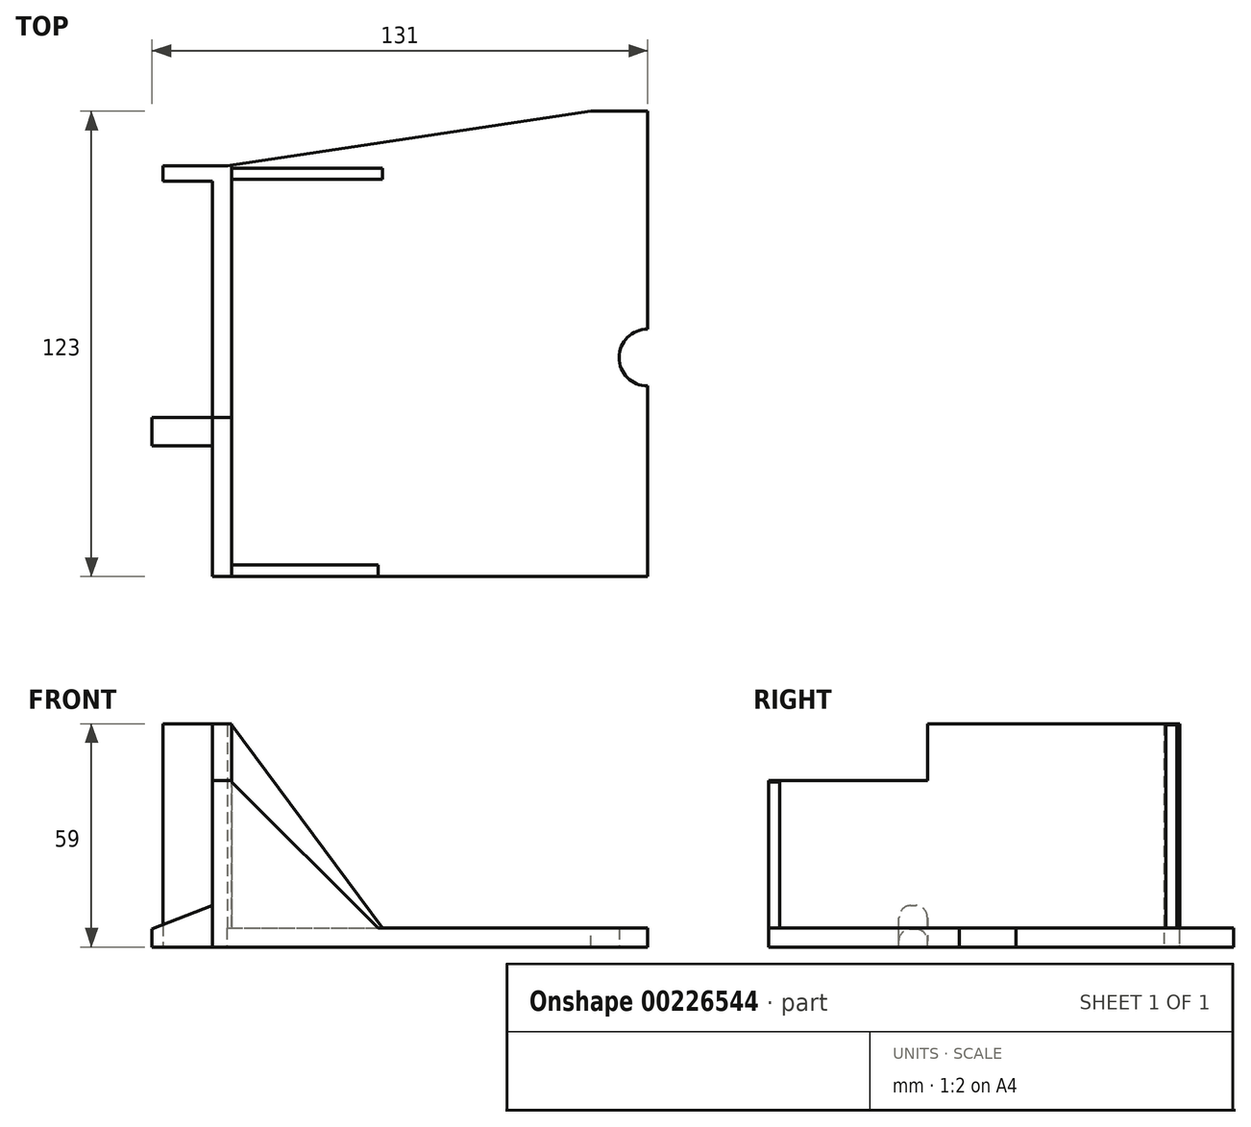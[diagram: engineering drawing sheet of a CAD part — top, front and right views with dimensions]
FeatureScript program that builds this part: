
annotation { "Feature Type Name" : "Feature", "Feature Type Description" : "" }
export const myFeature = defineFeature(function(context is Context, id is Id, definition is map)
    precondition{}
    {
        {
            var Q0;
            Q0=qCreatedBy(makeId("Top.planeOp"),FACE);
            var sketch = newSketch(context, id + "F0", { "sketchPlane" : qUnion([Q0])});
            skLineSegment(sketch, "E0.bottom", {"start": v(57.5, 61.5) * mm, "end": v(-57.5, 61.5) * mm});
            skLineSegment(sketch, "E0.top", {"start": v(57.5, -61.5) * mm, "end": v(-57.5, -61.5) * mm});
            skLineSegment(sketch, "E0.left", {"start": v(57.5, 61.5) * mm, "end": v(57.5, -61.5) * mm});
            skLineSegment(sketch, "E0.right", {"start": v(-57.5, 61.5) * mm, "end": v(-57.5, -61.5) * mm});
            skPoint(sketch, "E0.middle", {"position": v(0, 0) * mm});
            skCircle(sketch, "E1", {"center": v(57.5, -3.62) * mm, "radius": 7.5 * mm});
            skSolve(sketch);
        }
        {
            var Q0;
            {var subQ4=sQuery(id+"F0.wireOp",EDGE,"E0.bottom");Q0=makeQuery(id+"F0.imprint","IMPRINT",FACE,{"disambiguationData":[TD([[makeQuery(id+"F0.imprint","IMPRINT",EDGE,{"derivedFrom":subQ4}),1.0]])]});}
            extrude(context, id + "F1", {"entities" : qUnion([Q0]), "depth" : 5 * mm});
        }
        {
            var Q0;
            Q0=makeQuery(id+"F1.opExtrude","SWEPT_EDGE",EDGE,{"disambiguationData":[OSD([sQuery(id+"F0.wireOp",EDGE,"E0.bottom"),sQuery(id+"F0.wireOp",EDGE,"E0.right")])]});
            chamfer(context, id + "F2", {"entities" : qUnion([Q0]), "chamferType" : ChamferType.TWO_OFFSETS, "width1" : 15 * mm, "oppositeDirection" : false, "width2" : 100 * mm, "tangentPropagation" : true});
        }
        {
            var Q0;
            Q0=makeQuery(id+"F1.opExtrude","CAP_FACE",FACE,{"disambiguationData":[OSD([sQuery(id+"F0.wireOp",EDGE,"E0.bottom"),sQuery(id+"F0.wireOp",EDGE,"E0.top"),sQuery(id+"F0.wireOp",EDGE,"E0.left"),sQuery(id+"F0.wireOp",EDGE,"E0.right"),sQuery(id+"F0.wireOp",EDGE,"E1")])],"isStart":false});
            var sketch = newSketch(context, id + "F3", { "sketchPlane" : qUnion([Q0])});
            skLineSegment(sketch, "E2.bottom", {"start": v(-57.5, 46.5) * mm, "end": v(-52.5, 46.5) * mm});
            skLineSegment(sketch, "E2.top", {"start": v(-57.5, -61.5) * mm, "end": v(-52.5, -61.5) * mm});
            skLineSegment(sketch, "E2.left", {"start": v(-57.5, 46.5) * mm, "end": v(-57.5, -61.5) * mm});
            skLineSegment(sketch, "E2.right", {"start": v(-52.5, 46.5) * mm, "end": v(-52.5, -61.5) * mm});
            skLineSegment(sketch, "E3.bottom", {"start": v(-52.5, 46.5) * mm, "end": v(-52.5, 46.5) * mm});
            skLineSegment(sketch, "E3.top", {"start": v(-52.5, 47.25) * mm, "end": v(-52.5, 47.25) * mm});
            skLineSegment(sketch, "E3.left", {"start": v(-52.5, 46.5) * mm, "end": v(-52.5, 47.25) * mm});
            skLineSegment(sketch, "E3.right", {"start": v(-52.5, 46.5) * mm, "end": v(-52.5, 47.25) * mm});
            skSolve(sketch);
        }
        {
            var Q0;
            Q0=makeQuery(id+"F3.imprint","IMPRINT",FACE,{"disambiguationData":[TD([[makeQuery(id+"F3.imprint","IMPRINT",EDGE,{"derivedFrom":sQuery(id+"F3.wireOp",EDGE,"E2.bottom")}),-1.0]])]});
            extrude(context, id + "F4", {"entities" : qUnion([Q0]), "operationType" : NewBodyOperationType.ADD, "depth" : 54 * mm});
        }
        {
            var Q0;
            Q0=makeQuery(id+"F4.opExtrude","SWEPT_FACE",FACE,{"disambiguationData":[OSD([sQuery(id+"F3.wireOp",EDGE,"E2.bottom")])]});
            var Q1;
            Q1=makeQuery(id+"F4.opExtrude","SWEPT_EDGE",EDGE,{"disambiguationData":[OSD([sQuery(id+"F0.wireOp",EDGE,"E0.bottom"),sQuery(id+"F0.wireOp",EDGE,"E0.top"),sQuery(id+"F0.wireOp",EDGE,"E0.left"),sQuery(id+"F0.wireOp",EDGE,"E0.right"),sQuery(id+"F0.wireOp",EDGE,"E1"),sQuery(id+"F3.wireOp",EDGE,"E2.bottom"),sQuery(id+"F3.wireOp",EDGE,"E2.left")])]});
            revolve(context, id + "F5", {"operationType" : NewBodyOperationType.ADD, "entities" : qUnion([Q0]), "axis" : qUnion([Q1]), "revolveType" : RevolveType.ONE_DIRECTION, "oppositeDirection" : true, "angle" : 7.98 * degree});
        }
        {
            var Q0;
            Q0=makeQuery(id+"F4.opExtrude","SWEPT_FACE",FACE,{"disambiguationData":[OSD([sQuery(id+"F3.wireOp",EDGE,"E2.right")])]});
            var sketch = newSketch(context, id + "F6", { "sketchPlane" : qUnion([Q0])});
            skLineSegment(sketch, "E4.bottom", {"start": v(-61.5, 59) * mm, "end": v(-19.5, 59) * mm});
            skLineSegment(sketch, "E4.top", {"start": v(-61.5, 44) * mm, "end": v(-19.5, 44) * mm});
            skLineSegment(sketch, "E4.left", {"start": v(-61.5, 59) * mm, "end": v(-61.5, 44) * mm});
            skLineSegment(sketch, "E4.right", {"start": v(-19.5, 59) * mm, "end": v(-19.5, 44) * mm});
            skSolve(sketch);
        }
        {
            var Q0;
            Q0=makeQuery(id+"F6.imprint","IMPRINT",FACE,{"disambiguationData":[TD([[makeQuery(id+"F6.imprint","IMPRINT",EDGE,{"derivedFrom":sQuery(id+"F6.wireOp",EDGE,"E4.bottom")}),1.0]])]});
            extrude(context, id + "F7", {"entities" : qUnion([Q0]), "operationType" : NewBodyOperationType.REMOVE, "oppositeDirection" : true, "depth" : 25 * mm});
        }
        {
            var Q0;
            Q0=makeQuery(id+"F4.boolean.opBoolean","MERGE",FACE,{"derivedFrom":[makeQuery(id+"F1.opExtrude","SWEPT_FACE",FACE,{"disambiguationData":[OSD([sQuery(id+"F0.wireOp",EDGE,"E0.right")])]}),makeQuery(id+"F4.opExtrude","SWEPT_FACE",FACE,{"disambiguationData":[OSD([sQuery(id+"F3.wireOp",EDGE,"E2.left")])]})]});
            var sketch = newSketch(context, id + "F8", { "sketchPlane" : qUnion([Q0])});
            skLineSegment(sketch, "E5.bottom", {"start": v(19.5, 0) * mm, "end": v(27, 0) * mm});
            skLineSegment(sketch, "E5.top", {"start": v(19.5, 11) * mm, "end": v(27, 11) * mm});
            skLineSegment(sketch, "E5.left", {"start": v(19.5, 0) * mm, "end": v(19.5, 11) * mm});
            skLineSegment(sketch, "E5.right", {"start": v(27, 0) * mm, "end": v(27, 11) * mm});
            skSolve(sketch);
        }
        {
            var Q0;
            Q0=makeQuery(id+"F8.imprint","IMPRINT",FACE,{"disambiguationData":[TD([[makeQuery(id+"F8.imprint","IMPRINT",EDGE,{"derivedFrom":sQuery(id+"F8.wireOp",EDGE,"E5.bottom")}),1.0]])]});
            extrude(context, id + "F9", {"entities" : qUnion([Q0]), "operationType" : NewBodyOperationType.ADD, "depth" : 16 * mm});
        }
        {
            var Q0;
            Q0=makeQuery(id+"F9.opExtrude","CAP_EDGE",EDGE,{"disambiguationData":[OSD([sQuery(id+"F8.wireOp",EDGE,"E5.top")])],"isStart":false});
            chamfer(context, id + "F10", {"entities" : qUnion([Q0]), "chamferType" : ChamferType.TWO_OFFSETS, "width1" : 16.1 * mm, "oppositeDirection" : false, "width2" : 6.2 * mm, "tangentPropagation" : true});
        }
        {
            var Q0;
            Q0=makeQuery(id+"F10.opChamfer","BLEND_EDGE",EDGE,{"blendedFrom":[makeQuery(id+"F9.opExtrude","CAP_EDGE",EDGE,{"disambiguationData":[OSD([sQuery(id+"F8.wireOp",EDGE,"E5.top")])],"isStart":false}),makeQuery(id+"F9.opExtrude","SWEPT_FACE",FACE,{"disambiguationData":[OSD([sQuery(id+"F8.wireOp",EDGE,"E5.right")])]})],"blendedInto":[makeQuery(id+"F9.opExtrude","SWEPT_FACE",FACE,{"disambiguationData":[OSD([sQuery(id+"F8.wireOp",EDGE,"E5.right")])]})]});
            var Q1;
            Q1=makeQuery(id+"F10.opChamfer","BLEND_EDGE",EDGE,{"blendedFrom":[makeQuery(id+"F9.opExtrude","CAP_EDGE",EDGE,{"disambiguationData":[OSD([sQuery(id+"F8.wireOp",EDGE,"E5.top")])],"isStart":false}),makeQuery(id+"F9.opExtrude","SWEPT_FACE",FACE,{"disambiguationData":[OSD([sQuery(id+"F8.wireOp",EDGE,"E5.left")])]})],"blendedInto":[makeQuery(id+"F9.opExtrude","SWEPT_FACE",FACE,{"disambiguationData":[OSD([sQuery(id+"F8.wireOp",EDGE,"E5.left")])]})]});
            fillet(context, id + "F11", {"entities" : qUnion([Q0, Q1]), "radius" : 3 * mm, "tangentPropagation" : true, "allowEdgeOverflow" : false});
        }
        {
            var Q0;
            Q0=qCreatedBy(makeId("Top.planeOp"),FACE);
            var sketch = newSketch(context, id + "F12", { "sketchPlane" : qUnion([Q0])});
            skLineSegment(sketch, "E6.bottom", {"start": v(-52.66, 43.06) * mm, "end": v(-70.66, 43.06) * mm});
            skLineSegment(sketch, "E6.top", {"start": v(-52.66, 47.06) * mm, "end": v(-70.66, 47.06) * mm});
            skLineSegment(sketch, "E6.left", {"start": v(-52.66, 43.06) * mm, "end": v(-52.66, 47.06) * mm});
            skLineSegment(sketch, "E6.right", {"start": v(-70.66, 43.06) * mm, "end": v(-70.66, 47.06) * mm});
            skSolve(sketch);
        }
        {
            var Q0;
            Q0 = qSketchRegion(id + "F12", true);
            extrude(context, id + "F13", {"entities" : qUnion([Q0]), "operationType" : NewBodyOperationType.ADD, "depth" : 59 * mm});
        }
        {
            var Q0;
            Q0=makeQuery(id+"F1.opExtrude","CAP_FACE",FACE,{"disambiguationData":[OSD([sQuery(id+"F0.wireOp",EDGE,"E0.bottom"),sQuery(id+"F0.wireOp",EDGE,"E0.top"),sQuery(id+"F0.wireOp",EDGE,"E0.left"),sQuery(id+"F0.wireOp",EDGE,"E0.right"),sQuery(id+"F0.wireOp",EDGE,"E1")])],"isStart":false});
            var sketch = newSketch(context, id + "F14", { "sketchPlane" : qUnion([Q0])});
            skLineSegment(sketch, "E7.bottom", {"start": v(-12.5, -61.5) * mm, "end": v(-52.5, -61.5) * mm});
            skLineSegment(sketch, "E7.top", {"start": v(-12.5, -58.5) * mm, "end": v(-52.5, -58.5) * mm});
            skLineSegment(sketch, "E7.left", {"start": v(-12.5, -61.5) * mm, "end": v(-12.5, -58.5) * mm});
            skLineSegment(sketch, "E7.right", {"start": v(-52.5, -61.5) * mm, "end": v(-52.5, -58.5) * mm});
            skLineSegment(sketch, "E8.bottom", {"start": v(-52.5, 46.5) * mm, "end": v(-12.5, 46.5) * mm});
            skLineSegment(sketch, "E8.top", {"start": v(-52.5, 43.5) * mm, "end": v(-12.5, 43.5) * mm});
            skLineSegment(sketch, "E8.left", {"start": v(-52.5, 46.5) * mm, "end": v(-52.5, 43.5) * mm});
            skLineSegment(sketch, "E8.right", {"start": v(-12.5, 46.5) * mm, "end": v(-12.5, 43.5) * mm});
            skSolve(sketch);
        }
        {
            var Q0;
            Q0 = qSketchRegion(id + "F14", true);
            extrude(context, id + "F15", {"entities" : qUnion([Q0]), "operationType" : NewBodyOperationType.ADD, "depth" : 38.7 * mm});
        }
        {
            var Q0;
            Q0=makeQuery(id+"F15.opExtrude","CAP_FACE",FACE,{"disambiguationData":[OSD([sQuery(id+"F14.wireOp",EDGE,"E8.bottom"),sQuery(id+"F14.wireOp",EDGE,"E8.top"),sQuery(id+"F14.wireOp",EDGE,"E8.left"),sQuery(id+"F14.wireOp",EDGE,"E8.right")])],"isStart":false});
            extrude(context, id + "F16", {"entities" : qUnion([Q0]), "operationType" : NewBodyOperationType.ADD, "depth" : 15.2 * mm});
        }
        {
            var Q0;
            Q0=makeQuery(id+"F15.opExtrude","CAP_EDGE",EDGE,{"disambiguationData":[OSD([sQuery(id+"F14.wireOp",EDGE,"E7.left")])],"isStart":false});
            var Q1;
            Q1=makeQuery(id+"F16.opExtrude","CAP_EDGE",EDGE,{"disambiguationData":[OSD([sQuery(id+"F14.wireOp",EDGE,"E8.right")])],"isStart":false});
            chamfer(context, id + "F17", {"entities" : qUnion([Q0, Q1]), "width" : 40 * mm, "tangentPropagation" : true});
        }
        {
            var Q0;
            {var subQ0=sQuery(id+"F14.wireOp",EDGE,"E8.right");Q0=makeQuery(id+"F17.opChamfer","BLEND_EDGE",EDGE,{"blendedFrom":[makeQuery(id+"F16.opExtrude","CAP_EDGE",EDGE,{"disambiguationData":[OSD([subQ0])],"isStart":false}),makeQuery(id+"F16.boolean.opBoolean","MERGE",FACE,{"derivedFrom":[makeQuery(id+"F15.opExtrude","SWEPT_FACE",FACE,{"disambiguationData":[OSD([subQ0])]}),makeQuery(id+"F16.opExtrude","SWEPT_FACE",FACE,{"disambiguationData":[OSD([subQ0])]})]})],"blendedInto":[makeQuery(id+"F16.boolean.opBoolean","MERGE",FACE,{"derivedFrom":[makeQuery(id+"F15.opExtrude","SWEPT_FACE",FACE,{"disambiguationData":[OSD([subQ0])]}),makeQuery(id+"F16.opExtrude","SWEPT_FACE",FACE,{"disambiguationData":[OSD([subQ0])]})]})]});}
            chamfer(context, id + "F18", {"entities" : qUnion([Q0]), "chamferType" : ChamferType.TWO_OFFSETS, "width1" : 14.1 * mm, "oppositeDirection" : false, "width2" : 57 * mm, "tangentPropagation" : true});
        }
    });
